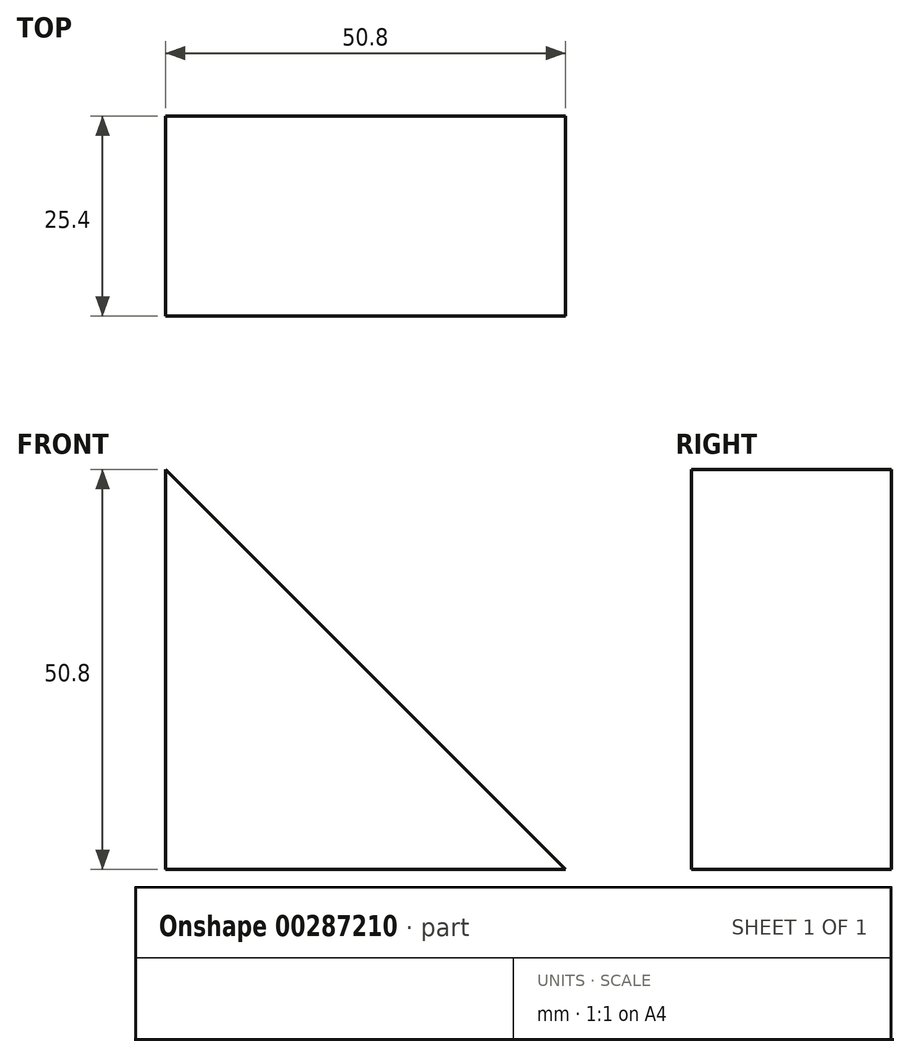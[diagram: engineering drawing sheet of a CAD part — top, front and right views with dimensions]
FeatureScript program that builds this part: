
annotation { "Feature Type Name" : "Feature", "Feature Type Description" : "" }
export const myFeature = defineFeature(function(context is Context, id is Id, definition is map)
    precondition{}
    {
        {
            var Q0;
            Q0=qCreatedBy(makeId("Front.planeOp"),FACE);
            var sketch = newSketch(context, id + "F0", { "sketchPlane" : qUnion([Q0])});
            skLineSegment(sketch, "E0", {"start": v(-47.36, 48.5) * mm, "end": v(-47.36, -2.3) * mm});
            skLineSegment(sketch, "E1", {"start": v(-47.36, -2.3) * mm, "end": v(3.44, -2.3) * mm});
            skLineSegment(sketch, "E2", {"start": v(3.44, -2.3) * mm, "end": v(-47.36, 48.5) * mm});
            skSolve(sketch);
        }
        {
            var Q0;
            Q0 = qSketchRegion(id + "F0", true);
            extrude(context, id + "F1", {"entities" : qUnion([Q0]), "depth" : 25.4 * mm});
        }
    });
